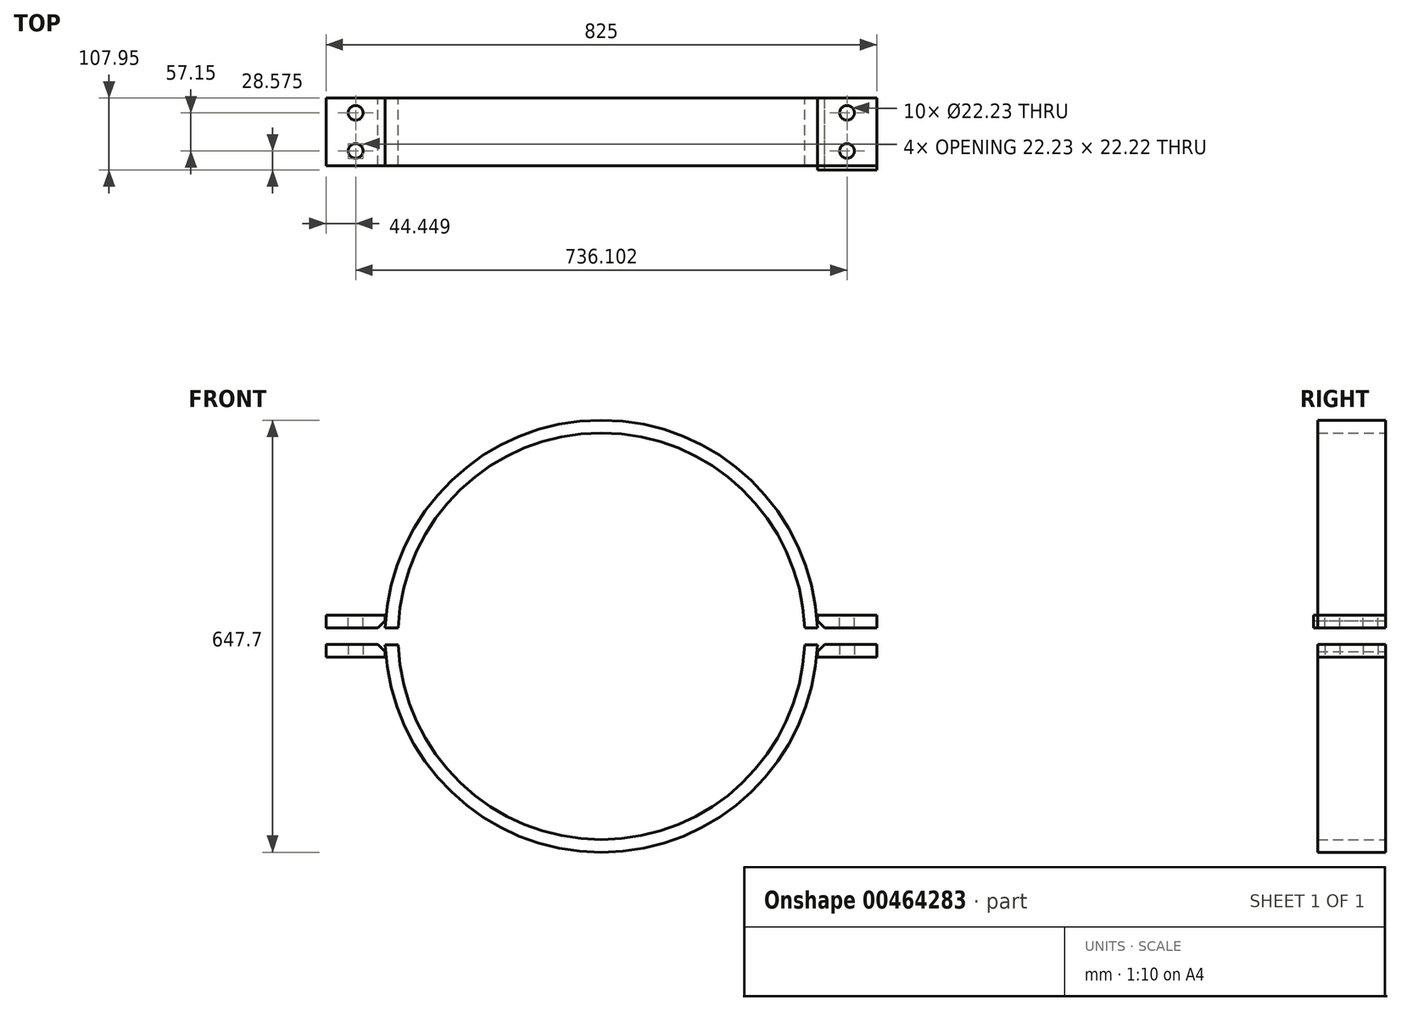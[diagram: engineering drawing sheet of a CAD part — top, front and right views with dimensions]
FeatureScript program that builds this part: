
annotation { "Feature Type Name" : "Feature", "Feature Type Description" : "" }
export const myFeature = defineFeature(function(context is Context, id is Id, definition is map)
    precondition{}
    {
        {
            var Q0;
            Q0=qCreatedBy(makeId("Front.planeOp"),FACE);
            var sketch = newSketch(context, id + "F0", { "sketchPlane" : qUnion([Q0])});
            skArc(sketch, "E0", {"start": v(304.54, 12.7) * mm, "mid": v(0, 304.8) * mm, "end": v(-304.54, 12.7) * mm});
            skArc(sketch, "E1", {"start": v(323.6, 12.7) * mm, "mid": v(0, 323.85) * mm, "end": v(-323.6, 12.7) * mm});
            skLineSegment(sketch, "E2", {"start": v(-323.6, 12.7) * mm, "end": v(-304.54, 12.7) * mm});
            skLineSegment(sketch, "E3.trimOffspring", {"start": v(304.54, 12.7) * mm, "end": v(323.6, 12.7) * mm});
            skSolve(sketch);
        }
        {
            var Q0;
            Q0 = qSketchRegion(id + "F0", true);
            extrude(context, id + "F1", {"entities" : qUnion([Q0]), "depth" : 101.6 * mm});
        }
        {
            var Q0;
            Q0=makeQuery(id+"F1.opExtrude","SWEPT_BODY",BODY,{"disambiguationData":[OSD([sQuery(id+"F0.wireOp",EDGE,"E0"),sQuery(id+"F0.wireOp",EDGE,"E1"),sQuery(id+"F0.wireOp",EDGE,"E2"),sQuery(id+"F0.wireOp",EDGE,"E3.trimOffspring")])]});
            var Q1;
            Q1=qCreatedBy(makeId("Top.planeOp"),FACE);
            mirror(context, id + "F2", {"entities" : qUnion([Q0]), "mirrorPlane" : qUnion([Q1])});
        }
        {
            var Q0;
            Q0=qCreatedBy(makeId("Front.planeOp"),FACE);
            var sketch = newSketch(context, id + "F3", { "sketchPlane" : qUnion([Q0])});
            skLineSegment(sketch, "E4", {"start": v(323.6, 23.39) * mm, "end": v(323.6, 31.64) * mm});
            skLineSegment(sketch, "E5", {"start": v(323.6, 31.64) * mm, "end": v(412.5, 31.64) * mm});
            skLineSegment(sketch, "E6", {"start": v(412.5, 31.64) * mm, "end": v(412.5, 12.6) * mm});
            skLineSegment(sketch, "E7", {"start": v(412.5, 12.6) * mm, "end": v(334.4, 12.6) * mm});
            skLineSegment(sketch, "E8", {"start": v(334.4, 12.6) * mm, "end": v(323.6, 23.39) * mm});
            skSolve(sketch);
        }
        {
            var Q0;
            Q0 = qSketchRegion(id + "F3", true);
            extrude(context, id + "F4", {"entities" : qUnion([Q0]), "operationType" : NewBodyOperationType.ADD, "depth" : 107.95 * mm});
        }
        {
            var Q0;
            Q0 = qSketchRegion(id + "F3", true);
            extrude(context, id + "F5", {"entities" : qUnion([Q0]), "depth" : 101.6 * mm});
        }
        {
            var Q0;
            Q0=makeQuery(id+"F5.opExtrude","SWEPT_FACE",FACE,{"disambiguationData":[OSD([sQuery(id+"F3.wireOp",EDGE,"E5")])]});
            var sketch = newSketch(context, id + "F6", { "sketchPlane" : qUnion([Q0])});
            skCircle(sketch, "E9", {"center": v(368.05, -22.23) * mm, "radius": 11.11 * mm});
            skLineSegment(sketch, "E10", {"start": v(323.6, -50.8) * mm, "end": v(412.5, -50.8) * mm, "construction": true});
            skCircle(sketch, "E11.MirrorC", {"center": v(368.05, -79.38) * mm, "radius": 11.11 * mm});
            skSolve(sketch);
        }
        {
            var Q0;
            Q0 = qSketchRegion(id + "F6", true);
            extrude(context, id + "F7", {"entities" : qUnion([Q0]), "operationType" : NewBodyOperationType.REMOVE, "oppositeDirection" : true, "depth" : 25.4 * mm});
        }
        {
            var Q0;
            Q0=makeQuery(id+"F5.opExtrude","SWEPT_BODY",BODY,{"disambiguationData":[OSD([sQuery(id+"F3.wireOp",EDGE,"E4"),sQuery(id+"F3.wireOp",EDGE,"E5"),sQuery(id+"F3.wireOp",EDGE,"E6"),sQuery(id+"F3.wireOp",EDGE,"E7"),sQuery(id+"F3.wireOp",EDGE,"E8")])]});
            var Q1;
            Q1=qCreatedBy(makeId("Right.planeOp"),FACE);
            mirror(context, id + "F8", {"entities" : qUnion([Q0]), "mirrorPlane" : qUnion([Q1])});
        }
        {
            var Q0;
            Q0=makeQuery(id+"F8.opPattern","COPY",BODY,{"derivedFrom":makeQuery(id+"F5.opExtrude","SWEPT_BODY",BODY,{"disambiguationData":[OSD([sQuery(id+"F3.wireOp",EDGE,"E4"),sQuery(id+"F3.wireOp",EDGE,"E5"),sQuery(id+"F3.wireOp",EDGE,"E6"),sQuery(id+"F3.wireOp",EDGE,"E7"),sQuery(id+"F3.wireOp",EDGE,"E8")])]}),"instanceName":"1"});
            var Q1;
            Q1=makeQuery(id+"F5.opExtrude","SWEPT_BODY",BODY,{"disambiguationData":[OSD([sQuery(id+"F3.wireOp",EDGE,"E4"),sQuery(id+"F3.wireOp",EDGE,"E5"),sQuery(id+"F3.wireOp",EDGE,"E6"),sQuery(id+"F3.wireOp",EDGE,"E7"),sQuery(id+"F3.wireOp",EDGE,"E8")])]});
            var Q2;
            Q2=qCreatedBy(makeId("Top.planeOp"),FACE);
            mirror(context, id + "F9", {"entities" : qUnion([Q0, Q1]), "mirrorPlane" : qUnion([Q2])});
        }
    });
